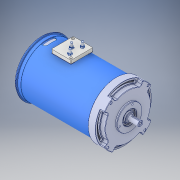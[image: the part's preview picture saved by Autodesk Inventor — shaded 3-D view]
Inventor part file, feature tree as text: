
AUTODESK INVENTOR PART (.ipt)
format: ipt  version: 2018 (Build 220112000, 112)  size: 3,288,064 bytes
history: mixed  units: mm
features: other x28, extrude x3, chamfer x3, sketch x3, projected_geometry x2, fillet x1, plane x1, delete_face x1, hole x1, imported_body x1
ambient origin geometry x8: Origin, YZ Plane, XZ Plane, XY Plane, X Axis, Y Axis, Z Axis, Center Point
bodies: Solid1 (imported_parasolid), Solid2 (imported_parasolid), Solid3 (imported_parasolid), Solid4 (imported_parasolid), Solid5 (imported_parasolid), Solid6 (imported_parasolid), Solid7 (imported_parasolid), Solid8 (imported_parasolid), Solid9 (imported_parasolid), Solid10 (imported_parasolid), Solid11 (imported_parasolid), Solid12 (imported_parasolid), Solid13 (imported_parasolid), Solid14 (imported_parasolid), Solid15 (imported_parasolid), Solid16 (imported_parasolid), Solid17 (imported_parasolid), Solid18 (imported_parasolid), Solid19 (imported_parasolid), Solid20 (imported_parasolid), Solid21 (imported_parasolid), Solid22 (imported_parasolid), Solid23 (imported_parasolid), Solid24 (imported_parasolid), Solid25 (imported_parasolid), Solid26 (imported_parasolid), Solid27 (imported_parasolid), Solid28 (imported_parasolid), Solid29 (imported_parasolid), Solid30 (imported_parasolid), Solid31 (imported_parasolid), Solid32 (imported_parasolid), Solid33 (imported_parasolid), Solid34 (imported_parasolid)
feature tree (44):
  extrude  "Extrusion1"  Depth=10.0mm TaperAngle=0.0deg
  extrude  "Extrusion2"  Depth=6.35mm TaperAngle=45.0deg
  fillet  "Fillet1"  Radius=6.35mm
  chamfer  "Chamfer1"  Distance=3.5052mm
  plane  "Work Plane1"
  delete_face  "Delete Face1"
  chamfer  "Chamfer2"  Distance=1.0mm Angle=45.0deg
  extrude  "Extrusion3"  Depth=10.0mm
  hole  "Hole1"  [1 undecoded]
  chamfer  "Chamfer3"  [1 undecoded]
  sketch  "Sketch1"  dims[d0=234.0mm d1=0.0mm d2=10.0mm d3=0.0mm]
  projected_geometry  "Projected Loop1"
  sketch  "Sketch2"  dims[d4=2.0mm d5=1.0mm d6=2.0mm d7=45.0deg d8=6.35mm]
  sketch  "Sketch3"  dims[d9=31.75mm d10=3.5052mm d11=0.0mm d12=1.0mm d13=2.0mm d14=45.0deg d15=10.0mm d16=10.0mm d17=9.144mm d18=12.7mm d19=4.0mm d20=2.0mm d21=90.0deg d22=15.875mm d23=20.594885mm d24=1.0mm d25=2.0mm d26=45.0deg]
  projected_geometry  "Projected Loop2"
  other  "Snap Ring for 1.375 Inch Shaft - Expanded (97633A360)-1-solid1"
  other  "184-9026-4-1-solid1"
  other  "6206_1-1_6206-1-solid1"
  other  "6206_1-1_6206 Bearing Seal-1-solid1"
  other  "6206_1-1_6206 Bearing Seal-2-solid1"
  other  "000-6210-1_000-6211-1-1-solid1"
  other  "000-6210-1_000-6211-1-2-solid1"
  other  "000-6210-1_000-6211-1-3-solid1"
  other  "000-6210-1_000-6212-1-1-solid1"
  other  "000-6210-1_000-6212-1-2-solid1"
  other  "000-6210-1_000-6212-1-3-solid1"
  other  "000-6210-1_6210-1-1-solid1"
  other  "6207-1_n024630a 004SYA9Q-1-solid1"
  other  "6207-1_n024630a 004SYA9Q_1-1-solid1"
  other  "6207-1_n024630a 004SYA9Q_2-1-solid1"
  other  "6207-1_n024630a 004SYA9Q_3-1-solid1"
  other  "6207-1_n024630a 004SYA9Q_4-1-solid1"
  other  "6207-1_n024630a 004SYA9Q_5-1-solid1"
  other  "6207-1_n024630a 004SYA9Q_6-1-solid1"
  other  "6207-1_n024630a 004SYA9Q_7-1-solid1"
  other  "6207-1_n024630a 004SYA9Q_8-1-solid1"
  other  "184-4026-1-1_184-2026-1-1-solid1"
  other  "Complete Encoder Assembly 1 Inch Bore-1_Encoder Base Plate-1-solid1"
  other  "Complete Encoder Assembly 1 Inch Bore-1_Encoder Reader Head-1-solid1"
  other  "184-7024-1-1_184-6044-6_1-1_184-6200-1-1-solid1"
  other  "184-7024-1-1_184-6044-6_1-1_184-6044-6-1-solid1"
  other  "184-1010-2.par-1-solid1"
  other  "Encoder Cover No Hole-1-solid1"
  imported_body  NMx_Import_Brep_tag  [imported B-rep: ~139 faces, bbox_mm=[0.0, 26.581891, 40.839252]]
note: 2 required parameter values undecoded (feature->parameter linkage not recoverable at this tier; creation-order binding heuristic only, values carry confidence <= 0.55)
